# Revit family: Building-SurfaceMountingEnclosures-GEWISS-44CE-JUNCTION-BOXES-WALL-MOUNTING_ROUND
name_source: partatom
category: Apparecchi elettrici
revit_build: Autodesk Revit 2016 (Build: 20161004_0715(x64)
units: mm (PartAtom-declared; Revit-internal decimal feet)

## family parameters
Condiviso = No
Host = Superficie
Mantenere orientamento annotazione = Sì
Numero OmniClass = 23.80.30.14.24
Punto di calcolo locali = Sì
Quota connettore circolare = Usa diametro
Taglio con vuoti quando caricato = No
Tipo di parte = Normale
Titolo OmniClass = Junction Boxes

## types (1)
- Building-SurfaceMountingEnclosures-GEWISS-44CE-JUNCTION-BOXES-WALL-MOUNTING_ROUND
    Accessories for insulation restoring = GW44622
    Application = Special uses
    Carico apparente = 0 VA
    Catalogue = BUILDING
    Catalogue Range = 44 CE
    Classificazione = Other
    Colour = Grey RAL 7035
    Corrugato = <Per categoria>
    Descrizione = JUNCT.BOX GLANDS D.80X40 IP44 GWT960°C
    Diametro scatola = 80 mm  [stored 0.262467 ft]
    EAN code = 8011564217720
    Electrocod = 02210
    Elemento di dettaglio = ELEMENTI DI DETTAGLIO 44CE-ROUND : Ø 80x40
    Entries No. holes / Ã˜ = 4 / 23
    Foro = 42 mm  [stored 0.137795 ft]
    GEWISS SCHEDA TECNICA = http://pro.gewiss.com
    Glow Wire Test = 960°C
    IDF = 281ef86f-a4be-434a-a055-bf78c4686e5f
    IDT = 7d4f1a4b-4295-41f9-b726-f05049c8eb16
    IP degree = IP44
    Immagine tipo = GW44001.jpg
    Insulation class = II (according to IEC 61140 standards)
    Internal dim. LxHxD (mm) = Ø 80x40
    Lid = Plain press-on
    Material = Technopolymer GWPLAST 75
    Modello = GW44052
    Operating temperature = -25 +60 °C
    Produttore = GEWISS S.p.A.
    Prospetto di default = 250 mm
    Raggio = 40 mm  [stored 0.131234 ft]
    Raggio coperchio = 45 mm
    SEO = Box
    Scatola = GEWISS SCATOLA
    Shock resistance = IK07
    Spessore = 35 mm
    Technical sheet = https://www.gewiss.com
    Thermo-pressure with ball = 85
    URL = https://www.gewiss.com
    Version file RFA = 18.0
    Voltaggio = 0 V
    Walls = With cable glands
    coperchio scatola = GEWISS COPERCHIO

note: source unit labels omitted for Thermo-pressure with ball — the stored unit's dimension contradicts the parameter name (converter mislabeling)

note: [stored X ft] marks values corroborated as IEEE doubles in the binary element streams (Revit-internal decimal feet)

## geometry (parser evidence)
native form markers: Blend x4, Sweep x1
no freeform markers — native parametric forms only
